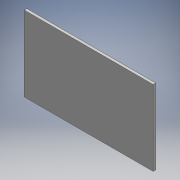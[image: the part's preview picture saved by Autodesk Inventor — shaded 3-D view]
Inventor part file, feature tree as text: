
AUTODESK INVENTOR PART (.ipt)
format: ipt  version: 2016 (Build 200138000, 138)  size: 83,456 bytes
history: native  units: mm
features: extrude x1, sketch x1
ambient origin geometry x8: Origin, YZ Plane, XZ Plane, XY Plane, X Axis, Y Axis, Z Axis, Center Point
bodies: Solid1 (feature_tree)
feature tree (2):
  extrude  "Extrusion1"  Depth=59.0mm
  sketch  "Sketch1"  dims[d0=101.0mm d1=59.0mm d2=2.0mm d3=0.0mm]
